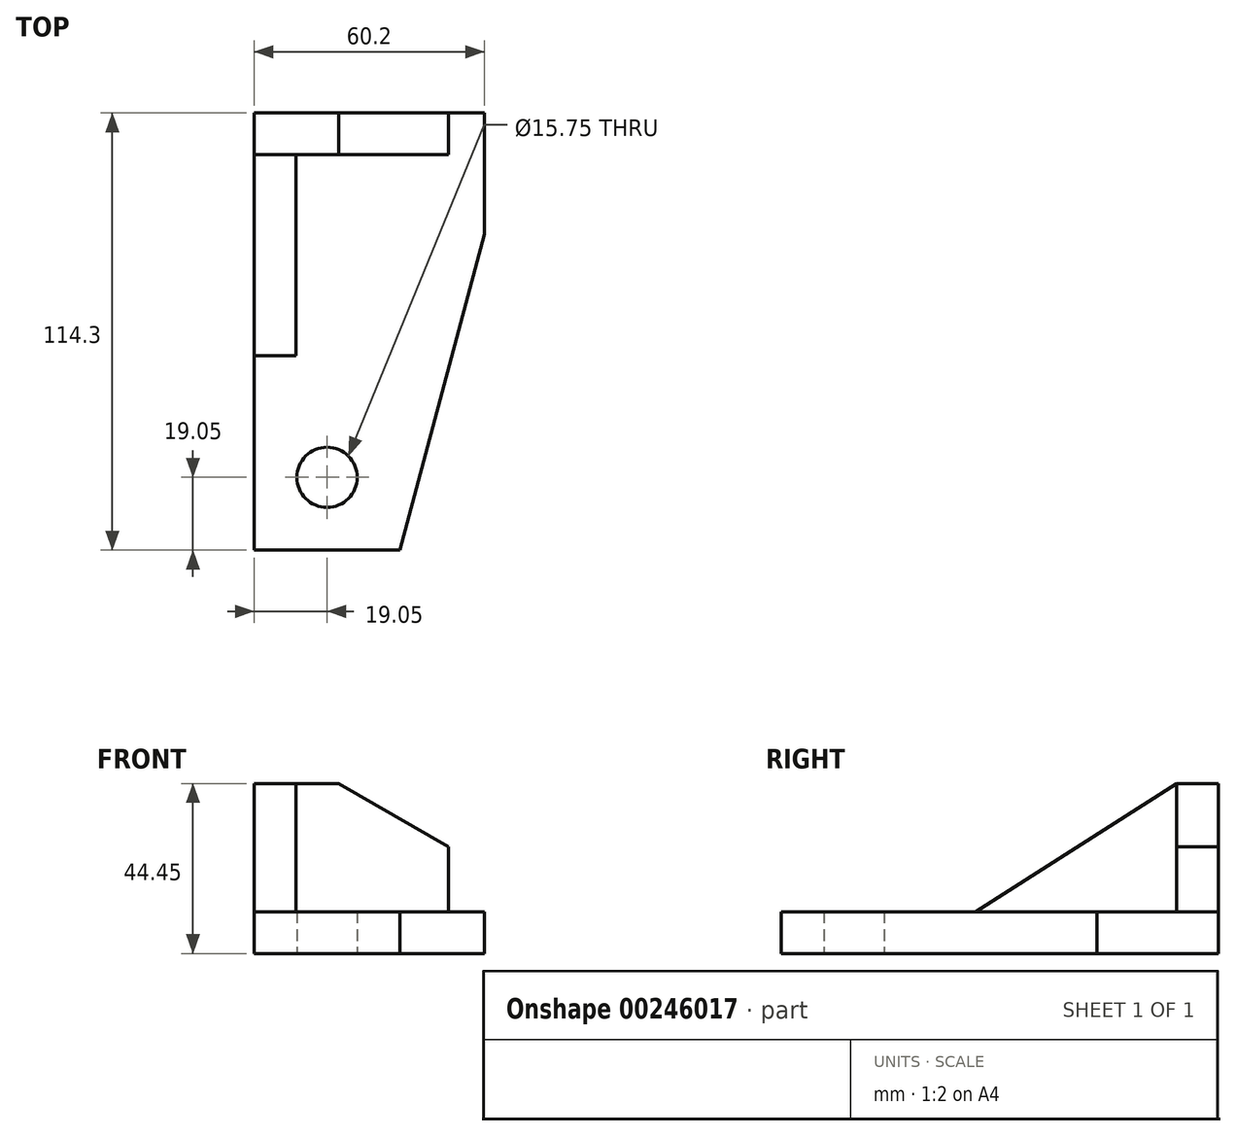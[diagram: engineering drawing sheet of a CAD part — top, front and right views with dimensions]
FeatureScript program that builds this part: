
annotation { "Feature Type Name" : "Feature", "Feature Type Description" : "" }
export const myFeature = defineFeature(function(context is Context, id is Id, definition is map)
    precondition{}
    {
        {
            var Q0;
            Q0=qCreatedBy(makeId("Top.planeOp"),FACE);
            var sketch = newSketch(context, id + "F0", { "sketchPlane" : qUnion([Q0])});
            skLineSegment(sketch, "E0.bottom", {"start": v(-19, 78.13) * mm, "end": v(41.19, 78.13) * mm});
            skLineSegment(sketch, "E0.top", {"start": v(-19, -36.17) * mm, "end": v(19.07, -36.17) * mm});
            skLineSegment(sketch, "E0.left", {"start": v(-19, 78.13) * mm, "end": v(-19, -36.17) * mm});
            skLineSegment(sketch, "E0.right", {"start": v(41.19, 78.13) * mm, "end": v(41.19, 46.38) * mm});
            skPoint(sketch, "E1", {"position": v(41.19, 46.38) * mm});
            skLineSegment(sketch, "E2", {"start": v(41.19, 46.38) * mm, "end": v(19.07, -36.17) * mm});
            skCircle(sketch, "E3", {"center": v(0.04, -17.12) * mm, "radius": 7.87 * mm});
            skPoint(sketch, "E4", {"position": v(6.57, -12.71) * mm});
            skSolve(sketch);
        }
        {
            var Q0;
            Q0 = qSketchRegion(id + "F0", true);
            extrude(context, id + "F1", {"entities" : qUnion([Q0]), "depth" : 10.92 * mm});
        }
        {
            var Q0;
            Q0=makeQuery(id+"F1.opExtrude","SWEPT_FACE",FACE,{"disambiguationData":[OSD([sQuery(id+"F0.wireOp",EDGE,"E0.bottom")])]});
            var sketch = newSketch(context, id + "F2", { "sketchPlane" : qUnion([Q0])});
            skLineSegment(sketch, "E5.bottom", {"start": v(-31.8, 10.92) * mm, "end": v(19, 10.92) * mm});
            skLineSegment(sketch, "E5.top", {"start": v(-3.09, 44.45) * mm, "end": v(19, 44.45) * mm});
            skPoint(sketch, "E6", {"position": v(-31.8, 10.92) * mm});
            skLineSegment(sketch, "E7", {"start": v(-31.8, 10.92) * mm, "end": v(-31.8, 27.88) * mm});
            skPoint(sketch, "E5.left.start.orphan", {"position": v(-41.19, 10.92) * mm});
            skLineSegment(sketch, "E8", {"start": v(19, 44.45) * mm, "end": v(19, 10.92) * mm});
            skPoint(sketch, "E9", {"position": v(19, 44.45) * mm});
            skPoint(sketch, "E10", {"position": v(-3.09, 44.45) * mm});
            skLineSegment(sketch, "E11", {"start": v(-3.09, 44.45) * mm, "end": v(-31.8, 27.88) * mm});
            skSolve(sketch);
        }
        {
            var Q0;
            Q0=makeQuery(id+"F2.imprint","IMPRINT",FACE,{"disambiguationData":[TD([[makeQuery(id+"F2.imprint","IMPRINT",EDGE,{"derivedFrom":sQuery(id+"F2.wireOp",EDGE,"E5.bottom")}),-1.0]])]});
            extrude(context, id + "F3", {"entities" : qUnion([Q0]), "operationType" : NewBodyOperationType.ADD, "oppositeDirection" : true, "depth" : 10.92 * mm});
        }
        {
            var Q0;
            Q0=makeQuery(id+"F3.boolean.opBoolean","MERGE",FACE,{"derivedFrom":[makeQuery(id+"F1.opExtrude","SWEPT_FACE",FACE,{"disambiguationData":[OSD([sQuery(id+"F0.wireOp",EDGE,"E0.left")])]}),makeQuery(id+"F3.opExtrude","SWEPT_FACE",FACE,{"disambiguationData":[OSD([sQuery(id+"F2.wireOp",EDGE,"E8")])]})]});
            var sketch = newSketch(context, id + "F4", { "sketchPlane" : qUnion([Q0])});
            skLineSegment(sketch, "E12.bottom", {"start": v(-67.2, 10.92) * mm, "end": v(-14.63, 10.92) * mm});
            skLineSegment(sketch, "E12.left", {"start": v(-67.2, 10.92) * mm, "end": v(-67.2, 44.45) * mm});
            skLineSegment(sketch, "E13", {"start": v(-67.2, 44.45) * mm, "end": v(-14.63, 10.92) * mm});
            skSolve(sketch);
        }
        {
            var Q0;
            Q0=makeQuery(id+"F4.imprint","IMPRINT",FACE,{"disambiguationData":[TD([[makeQuery(id+"F4.imprint","IMPRINT",EDGE,{"derivedFrom":sQuery(id+"F4.wireOp",EDGE,"E12.bottom")}),1.0]])]});
            extrude(context, id + "F5", {"entities" : qUnion([Q0]), "oppositeDirection" : true, "depth" : 10.92 * mm});
        }
    });
